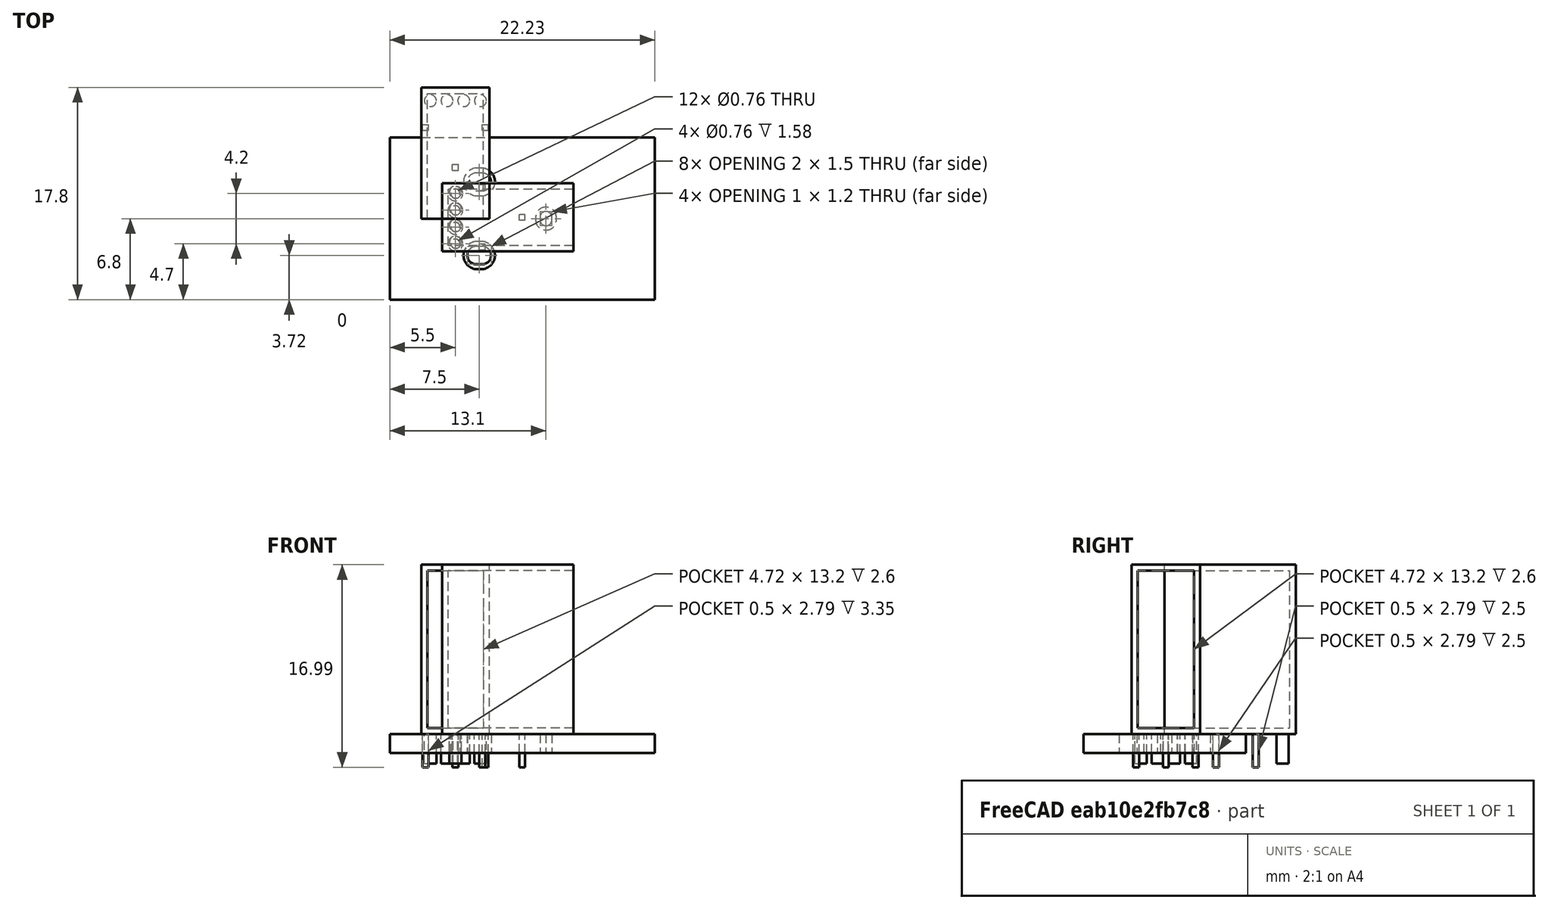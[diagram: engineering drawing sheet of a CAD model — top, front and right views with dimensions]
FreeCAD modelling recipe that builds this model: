
FCSTD DOCUMENT  (FreeCAD 0.19R18353 (Git))
Label: assembly
License: All rights reserved
LicenseURL: http://en.wikipedia.org/wiki/All_rights_reserved
objects: Part::Box×5, Part::FeaturePython×5, Part::Cylinder×4, Part::Cut×1, App::DocumentObjectGroup×1, Part::Feature×1
note: 16 computed .brp shape members not serialized (recipe doc carries the construction recipe); baked Part::Feature solids carry a one-line shape summary decoded from their .brp

FEATURE [Part::Box] cube
  AttacherType = Attacher::AttachEngine3D
  Height = 14.2
  Length = 5.72
  Width = 11
FEATURE [Part::Box] cube001
  AttacherType = Attacher::AttachEngine3D
  Height = 13.2
  Length = 4.72
  Placement = pos=(0.5,-0.5,0.5) rot=(0,0,1;0rad)
  Width = 11
FEATURE [Part::Cut] difference
  Base = -> cube
  Placement = pos=(-2.86,0,0) rot=(0,0,1;0rad)
  Tool = -> cube001
FEATURE [Part::Box] cube002
  AttacherType = Attacher::AttachEngine3D
  Height = 2.79
  Length = 0.5
  Placement = pos=(2.25,7.4,-2.79) rot=(0,0,1;0rad)
  Width = 0.5
FEATURE [Part::Box] cube003
  AttacherType = Attacher::AttachEngine3D
  Height = 2.79
  Length = 0.5
  Placement = pos=(-2.75,7.4,-2.79) rot=(0,0,1;0rad)
  Width = 0.5
FEATURE [Part::Box] cube004
  AttacherType = Attacher::AttachEngine3D
  Height = 2.79
  Length = 0.5
  Placement = pos=(-0.25,4.05,-2.79) rot=(0,0,1;0rad)
  Width = 0.5
FEATURE [Part::Cylinder] cylinder
  Angle = 360
  AttacherType = Attacher::AttachEngine3D
  Height = 2.5
  Placement = pos=(0.7,9.9,-2.5) rot=(0,0,1;0rad)
  Radius = 0.5
FEATURE [Part::Cylinder] cylinder001
  Angle = 360
  AttacherType = Attacher::AttachEngine3D
  Height = 2.5
  Placement = pos=(2.1,9.9,-2.5) rot=(0,0,1;0rad)
  Radius = 0.5
FEATURE [Part::Cylinder] cylinder002
  Angle = 360
  AttacherType = Attacher::AttachEngine3D
  Height = 2.5
  Placement = pos=(-0.7,9.9,-2.5) rot=(0,0,1;0rad)
  Radius = 0.5
FEATURE [Part::Cylinder] cylinder003
  Angle = 360
  AttacherType = Attacher::AttachEngine3D
  Height = 2.5
  Placement = pos=(-2.1,9.9,-2.5) rot=(0,0,1;0rad)
  Radius = 0.5
FEATURE [Part::FeaturePython] Filk_lines  label="FrontSilk"  # a2plus imported part (geometry in sourceFile) (typed FeaturePython)
  fixedPosition = true
FEATURE [Part::FeaturePython] TopPads  # a2plus imported part (geometry in sourceFile) (typed FeaturePython)
  fixedPosition = true
FEATURE [Part::FeaturePython] BotPads  # a2plus imported part (geometry in sourceFile) (typed FeaturePython)
  fixedPosition = true
FEATURE [Part::FeaturePython] THPs  label="PTHs"  # a2plus imported part (geometry in sourceFile) (typed FeaturePython)
  fixedPosition = true
FEATURE [Part::FeaturePython] newPCB  label="Pcb"  # a2plus imported part (geometry in sourceFile) (typed FeaturePython)
  fixedPosition = true
FEATURE [App::DocumentObjectGroup] USB_A_90_fp
  Group = -> [Filk_lines,TopPads,BotPads,THPs,newPCB]
FEATURE [Part::Feature] Shape001  label="Fusion"
  shape: bbox 11 x 5.72 x 16.99 mm, 34 faces (baked)
